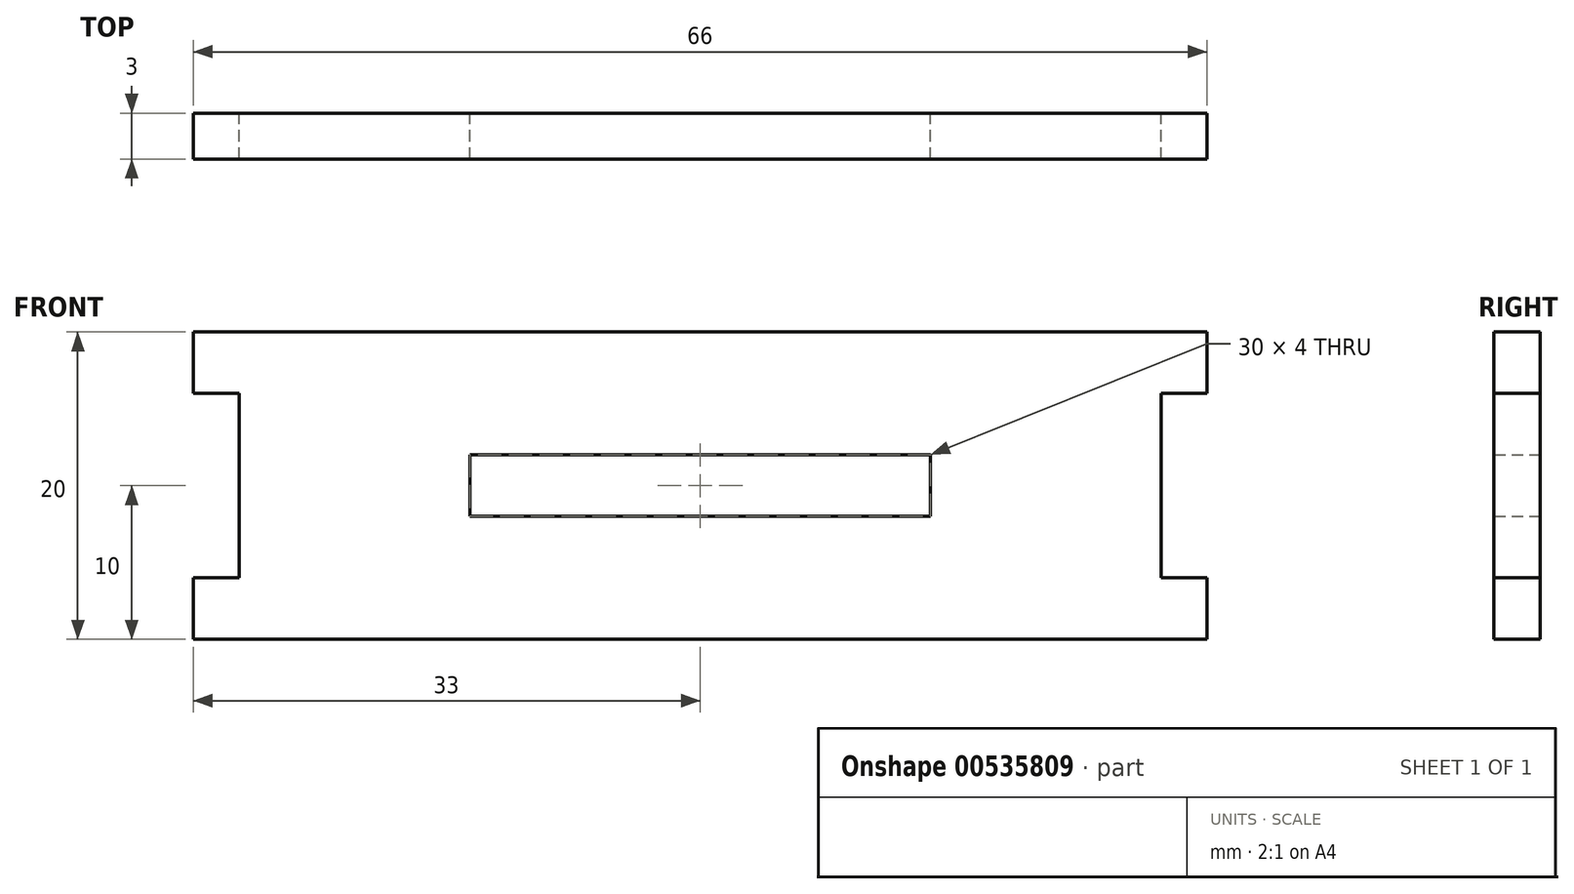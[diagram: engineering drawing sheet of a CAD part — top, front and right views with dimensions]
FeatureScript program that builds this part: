
annotation { "Feature Type Name" : "Feature", "Feature Type Description" : "" }
export const myFeature = defineFeature(function(context is Context, id is Id, definition is map)
    precondition{}
    {
        {
            var Q0;
            Q0=qCreatedBy(makeId("Front.planeOp"),FACE);
            var sketch = newSketch(context, id + "F0", { "sketchPlane" : qUnion([Q0])});
            skLineSegment(sketch, "E0.bottom", {"start": v(-33, 10) * mm, "end": v(33, 10) * mm});
            skLineSegment(sketch, "E0.top", {"start": v(-33, -10) * mm, "end": v(33, -10) * mm});
            skLineSegment(sketch, "E0.left", {"start": v(-33, 10) * mm, "end": v(-33, 6) * mm});
            skLineSegment(sketch, "E0.right", {"start": v(33, 10) * mm, "end": v(33, 6) * mm});
            skPoint(sketch, "E0.middle", {"position": v(0, 0) * mm});
            skLineSegment(sketch, "E1", {"start": v(-33, 6) * mm, "end": v(-30, 6) * mm});
            skLineSegment(sketch, "E2.MirrorCS", {"start": v(33, 6) * mm, "end": v(30, 6) * mm});
            skLineSegment(sketch, "E3.MirrorCS", {"start": v(-33, -6) * mm, "end": v(-30, -6) * mm});
            skLineSegment(sketch, "E4.MirrorCS", {"start": v(33, -6) * mm, "end": v(30, -6) * mm});
            skLineSegment(sketch, "E5", {"start": v(-30, 6) * mm, "end": v(-30, -6) * mm});
            skLineSegment(sketch, "E6", {"start": v(30, 6) * mm, "end": v(30, -6) * mm});
            skLineSegment(sketch, "E7.trimOffspring", {"start": v(-33, -6) * mm, "end": v(-33, -10) * mm});
            skLineSegment(sketch, "E8.trimOffspring", {"start": v(33, -6) * mm, "end": v(33, -10) * mm});
            skLineSegment(sketch, "E9.bottom", {"start": v(-15, 2) * mm, "end": v(15, 2) * mm});
            skLineSegment(sketch, "E9.top", {"start": v(-15, -2) * mm, "end": v(15, -2) * mm});
            skLineSegment(sketch, "E9.left", {"start": v(-15, 2) * mm, "end": v(-15, -2) * mm});
            skLineSegment(sketch, "E9.right", {"start": v(15, 2) * mm, "end": v(15, -2) * mm});
            skSolve(sketch);
        }
        {
            var Q0;
            Q0=makeQuery(id+"F0.imprint","IMPRINT",FACE,{"disambiguationData":[TD([[makeQuery(id+"F0.imprint","IMPRINT",EDGE,{"derivedFrom":sQuery(id+"F0.wireOp",EDGE,"E0.bottom")}),-1.0]])]});
            extrude(context, id + "F1", {"entities" : qUnion([Q0]), "depth" : 3 * mm, "offsetDistance" : 25 * mm});
        }
    });
